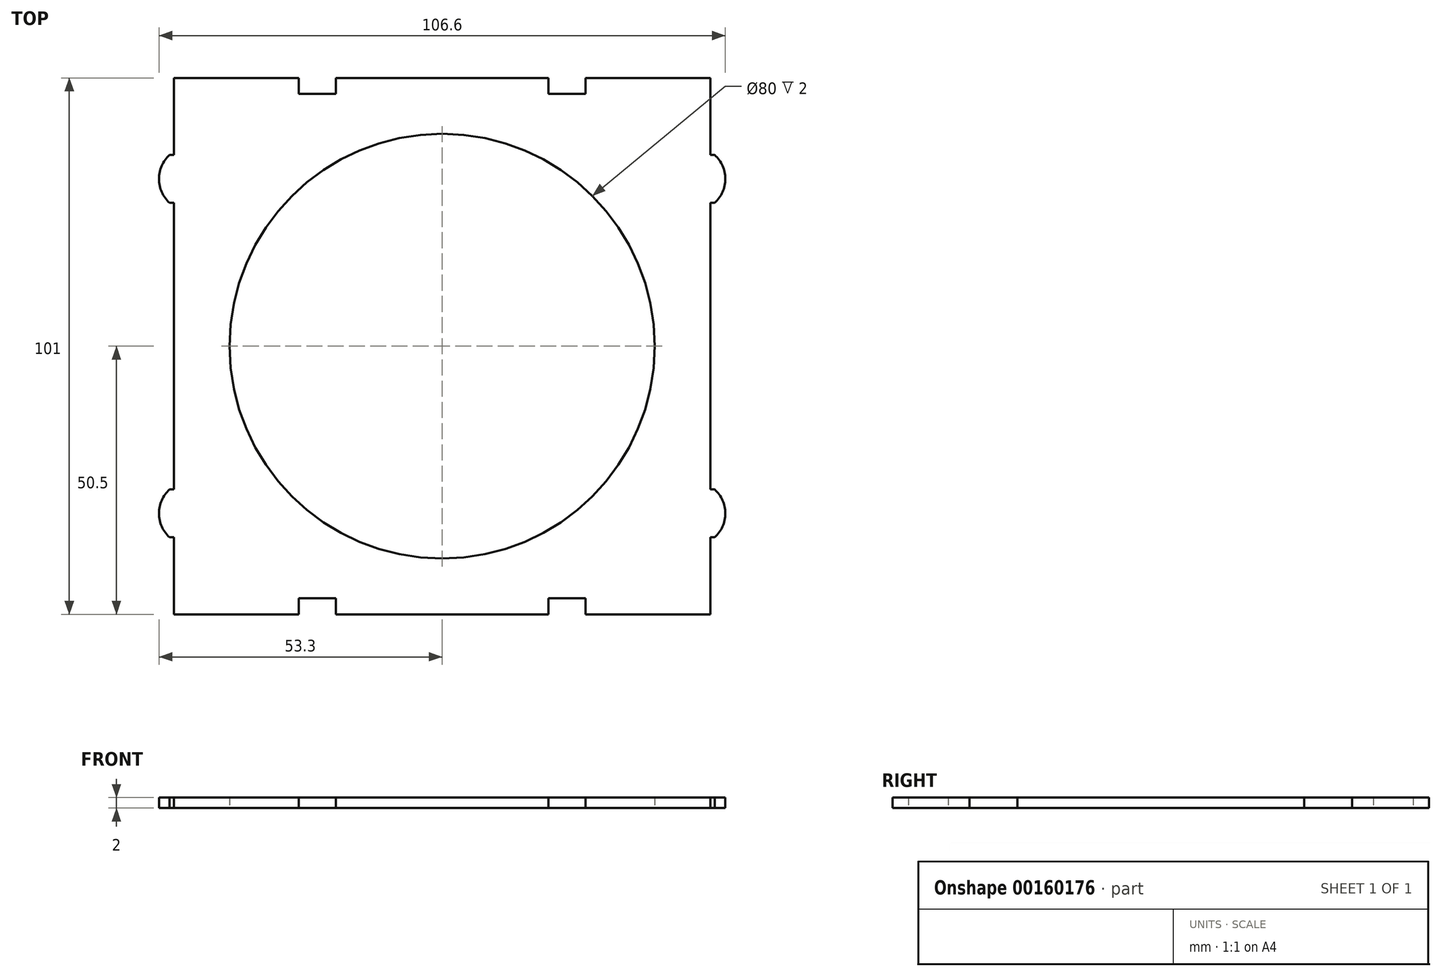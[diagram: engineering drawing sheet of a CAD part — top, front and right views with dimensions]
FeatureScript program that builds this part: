
annotation { "Feature Type Name" : "Feature", "Feature Type Description" : "" }
export const myFeature = defineFeature(function(context is Context, id is Id, definition is map)
    precondition{}
    {
        {
            var Q0;
            Q0=qCreatedBy(makeId("Top.planeOp"),FACE);
            var sketch = newSketch(context, id + "F0", { "sketchPlane" : qUnion([Q0])});
            skLineSegment(sketch, "E0.bottom", {"start": v(50.5, 50.5) * mm, "end": v(27, 50.5) * mm});
            skLineSegment(sketch, "E0.top", {"start": v(50.5, -50.5) * mm, "end": v(27, -50.5) * mm});
            skLineSegment(sketch, "E0.left", {"start": v(50.5, 50.5) * mm, "end": v(50.5, 36) * mm});
            skLineSegment(sketch, "E0.right", {"start": v(-50.5, 50.5) * mm, "end": v(-50.5, 36) * mm});
            skPoint(sketch, "E0.middle", {"position": v(0, 0) * mm});
            skCircle(sketch, "E1", {"center": v(0, 0) * mm, "radius": 40 * mm});
            skPoint(sketch, "E2", {"position": v(-50.5, -31.5) * mm});
            skPoint(sketch, "E3", {"position": v(50.5, -31.5) * mm});
            skPoint(sketch, "E4", {"position": v(50.5, 31.5) * mm});
            skPoint(sketch, "E5", {"position": v(-50.5, 0) * mm});
            skPoint(sketch, "E6", {"position": v(50.5, 0) * mm});
            skPoint(sketch, "E7.middle", {"position": v(-50.5, 31.5) * mm});
            skLineSegment(sketch, "E8.trimOffspring", {"start": v(-50.5, -36) * mm, "end": v(-50.5, -50.5) * mm});
            skLineSegment(sketch, "E9.trimOffspring", {"start": v(50.5, -36) * mm, "end": v(50.5, -50.5) * mm});
            skLineSegment(sketch, "E10.bottom", {"start": v(-50.5, 36) * mm, "end": v(-51.3, 36) * mm});
            skLineSegment(sketch, "E10.top", {"start": v(-50.5, 27) * mm, "end": v(-51.3, 27) * mm});
            skLineSegment(sketch, "E11.top", {"start": v(-50.8, 36) * mm, "end": v(-51.3, 36) * mm});
            skPoint(sketch, "E12", {"position": v(-53.3, 31.5) * mm});
            skArc(sketch, "E13", {"start": v(-51.3, 36) * mm, "mid": v(-53.3, 31.5) * mm, "end": v(-51.3, 27) * mm});
            skPoint(sketch, "E14.orphan", {"position": v(-53.3, 36) * mm});
            skPoint(sketch, "E15.orphan", {"position": v(-53.3, 27) * mm});
            skLineSegment(sketch, "E16.MirrorCS", {"start": v(-50.5, -27) * mm, "end": v(-51.3, -27) * mm});
            skArc(sketch, "E17.MirrorCS", {"start": v(-51.3, -36) * mm, "mid": v(-53.3, -31.5) * mm, "end": v(-51.3, -27) * mm});
            skLineSegment(sketch, "E18.MirrorCS", {"start": v(-50.5, -36) * mm, "end": v(-51.3, -36) * mm});
            skPoint(sketch, "E19.MirrorCS.end.orphan", {"position": v(50.5, 27) * mm});
            skPoint(sketch, "E19.MirrorCS.start.orphan", {"position": v(50.5, 36) * mm});
            skLineSegment(sketch, "E20.MirrorCS", {"start": v(50.5, 36) * mm, "end": v(51.3, 36) * mm});
            skArc(sketch, "E21.MirrorCS", {"start": v(51.3, 36) * mm, "mid": v(53.3, 31.5) * mm, "end": v(51.3, 27) * mm});
            skLineSegment(sketch, "E22.MirrorCS", {"start": v(50.5, 27) * mm, "end": v(51.3, 27) * mm});
            skLineSegment(sketch, "E23.MirrorCS", {"start": v(50.5, -27) * mm, "end": v(51.3, -27) * mm});
            skArc(sketch, "E24.MirrorCS", {"start": v(51.3, -36) * mm, "mid": v(53.3, -31.5) * mm, "end": v(51.3, -27) * mm});
            skLineSegment(sketch, "E25.MirrorCS", {"start": v(50.5, -36) * mm, "end": v(51.3, -36) * mm});
            skLineSegment(sketch, "E26", {"start": v(-50.5, 36) * mm, "end": v(-50.5, 27) * mm});
            skLineSegment(sketch, "E27.top", {"start": v(-27, 47.5) * mm, "end": v(-20, 47.5) * mm});
            skLineSegment(sketch, "E27.left", {"start": v(-27, 50.5) * mm, "end": v(-27, 47.5) * mm});
            skLineSegment(sketch, "E27.right", {"start": v(-20, 50.5) * mm, "end": v(-20, 47.5) * mm});
            skLineSegment(sketch, "E28.trimOffspring", {"start": v(-27, 50.5) * mm, "end": v(-50.5, 50.5) * mm});
            skPoint(sketch, "E29.trimOffspring.end.orphan", {"position": v(-50.5, -27) * mm});
            skLineSegment(sketch, "E30", {"start": v(-50.5, 27) * mm, "end": v(-50.5, -27) * mm});
            skPoint(sketch, "E31.trimOffspring.end.orphan", {"position": v(50.5, -27) * mm});
            skLineSegment(sketch, "E32", {"start": v(50.5, 27) * mm, "end": v(50.5, -27) * mm});
            skLineSegment(sketch, "E33.MirrorCS", {"start": v(27, 50.5) * mm, "end": v(27, 47.5) * mm});
            skLineSegment(sketch, "E34.MirrorCS", {"start": v(27, 47.5) * mm, "end": v(20, 47.5) * mm});
            skLineSegment(sketch, "E35.MirrorCS", {"start": v(20, 50.5) * mm, "end": v(20, 47.5) * mm});
            skLineSegment(sketch, "E36.trimOffspring", {"start": v(20, 50.5) * mm, "end": v(-20, 50.5) * mm});
            skLineSegment(sketch, "E37.MirrorCS", {"start": v(-27, -50.5) * mm, "end": v(-27, -47.5) * mm});
            skLineSegment(sketch, "E38.MirrorCS", {"start": v(-27, -47.5) * mm, "end": v(-20, -47.5) * mm});
            skLineSegment(sketch, "E39.MirrorCS", {"start": v(-20, -50.5) * mm, "end": v(-20, -47.5) * mm});
            skLineSegment(sketch, "E40.MirrorCS", {"start": v(20, -50.5) * mm, "end": v(20, -47.5) * mm});
            skLineSegment(sketch, "E41.MirrorCS", {"start": v(27, -47.5) * mm, "end": v(20, -47.5) * mm});
            skLineSegment(sketch, "E42.MirrorCS", {"start": v(27, -50.5) * mm, "end": v(27, -47.5) * mm});
            skLineSegment(sketch, "E43.trimOffspring", {"start": v(-27, -50.5) * mm, "end": v(-50.5, -50.5) * mm});
            skLineSegment(sketch, "E44.trimOffspring", {"start": v(20, -50.5) * mm, "end": v(-20, -50.5) * mm});
            skSolve(sketch);
        }
        {
            var Q0;
            Q0=makeQuery(id+"F0.imprint","IMPRINT",FACE,{"disambiguationData":[TD([[makeQuery(id+"F0.imprint","IMPRINT",EDGE,{"derivedFrom":sQuery(id+"F0.wireOp",EDGE,"E0.bottom")}),1.0]])]});
            var Q1;
            Q1=makeQuery(id+"F0.imprint","IMPRINT",FACE,{"disambiguationData":[TD([[makeQuery(id+"F0.imprint","IMPRINT",EDGE,{"derivedFrom":sQuery(id+"F0.wireOp",EDGE,"E10.top")}),-1.0]])]});
            extrude(context, id + "F1", {"entities" : qUnion([Q0, Q1]), "depth" : 2 * mm});
        }
    });
